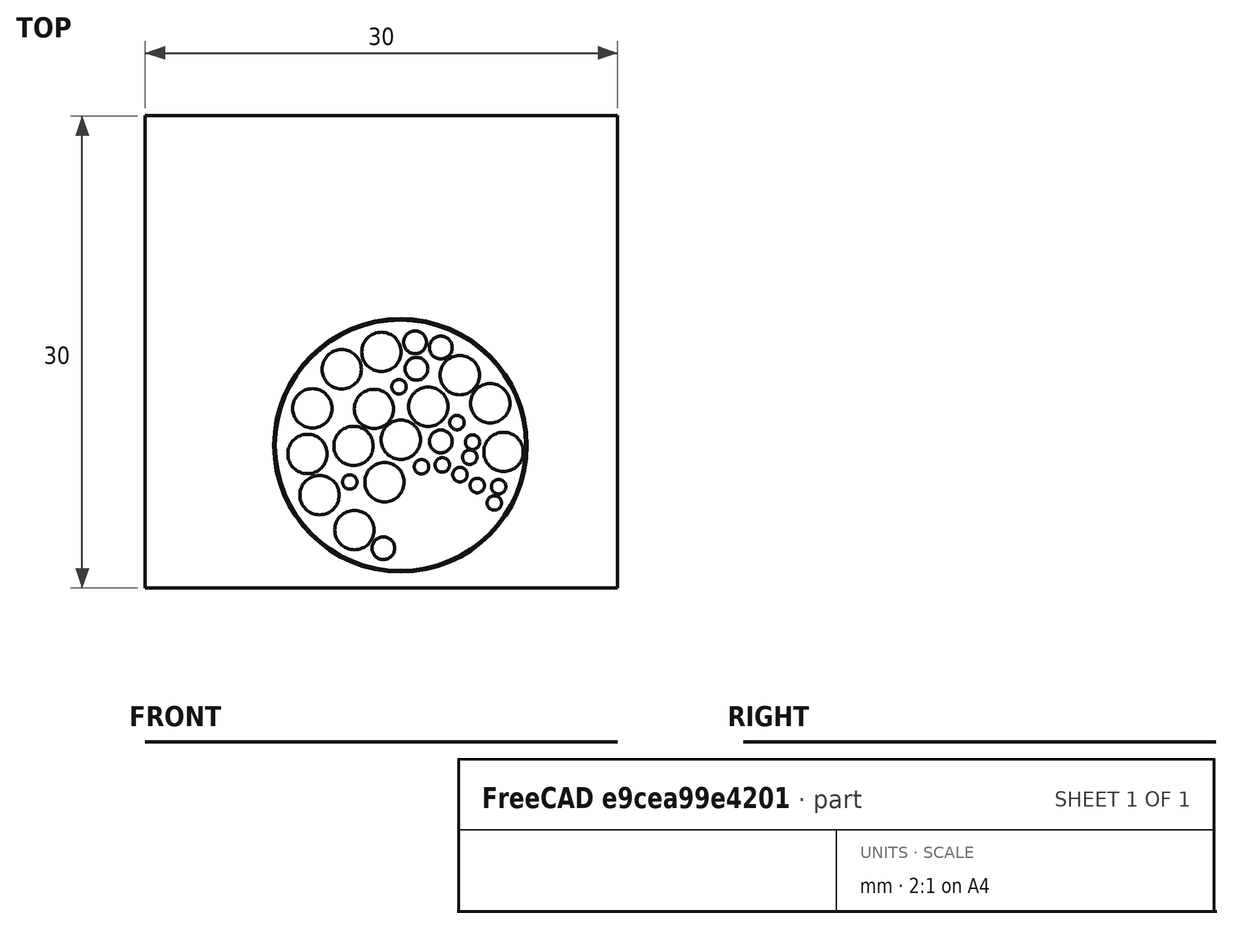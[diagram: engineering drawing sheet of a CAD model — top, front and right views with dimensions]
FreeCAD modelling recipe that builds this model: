
FCSTD DOCUMENT  (FreeCAD 0.21R33668 +26 (Git))
Label: realistic_case_with_dielectrics_fdtd_cell
License: All rights reserved
LicenseURL: http://en.wikipedia.org/wiki/All_rights_reserved
objects: Part::Part2DObjectPython×98, Part::Cut×3, Spreadsheet::Sheet×1, Part::MultiFuse×1
note: 102 computed .brp shape members not serialized (recipe doc carries the construction recipe); baked Part::Feature solids carry a one-line shape summary decoded from their .brp

FEATURE [Part::Part2DObjectPython] Circle006  label="Overbraid_internal"  # Draft 2D object (typed FeaturePython)
  Area = 203.583
  FirstAngle = 0
  LastAngle = 0
  MakeFace = true
  Radius = 8.05
  expr: Radius = <<Spreadsheet>>.OJ_outer_radius
FEATURE [Spreadsheet::Sheet] Spreadsheet
  cells = C1='Radius; D1='Insulation O.R.; G1='Dx; H1='Dy; B2='Overbraid Jacket (OJ); C2(OJ_radius)=7.95; D2(OJ_outer_radius)=8.05; F2='FDTD Cell; G2(fdtd_cell_Lx)==30 mm; H2(FDTD_Cell_Ly)==30 mm; B3='Shield (S); C3(S_radius)==4.5 / 2; F3='Inner region; G3(Inner_region_Dx)=16.5; H3(Inner_region_Dy)==G3; B4='AWG 11; C4(AWG11)==2.3 / 2; D4(awg11_insulation_radius)==C4 + 0.1; G4='Xmax; H4='Xmin; I4='Ymax; J4='Ymin; B5='AWG 17; C5(AWG17)==1.15 / 2; D5(awg17_insulation_radius)==C5 + 0.15; F5='Bounding box; G5==C15 + C4; H5==C12 - C4; I5==D38 + D5; J5==D52 - C3; B6='AWG 21; C6(AWG21)==0.72 / 2; D6(awg21_insulation_radius)==C6 + 0.1; G6==G5 - H5; I6==I5 - J5; A8='Num; B8='AWG 11; C8='x; D8='y; A9=0; B9='A; C9(AWG_11_A_x)==-1.209 mm; D9(AWG_11_A_y)==5.934 mm; A10=1; B10='B; C10(AWG_11_B_x)==-3.734 mm; D10(AWG_11_B_y)=4.83; A11=2; B11='C; C11(AWG_11_C_x)==-5.595; D11(AWG_11_C_y)=2.349; A12=3; B12='D; C12(AWG_11_D_x)==-5.905; D12(AWG_11_D_y)==-0.548; A13=4; B13='E; C13(AWG_11_E_x)==-5.141; D13(AWG_11_E_y)==-3.16; A14=5; B14='F; C14(AWG_11_F_x)==-2.923; D14(AWG_11_F_y)==-5.378; A15=6; B15='G; C15(AWG_11_G_x)=6.545; D15(AWG_11_G_y)==-0.417; A16=7; B16='H; C16(AWG_11_H_x)=5.699; D16(AWG_11_H_y)=2.671; A17=8; B17='I; C17(AWG_11_I_x)=3.767; D17(AWG_11_I_y)=4.46; A18=9; B18='J; C18(AWG_11_J_x)=1.763; D18(AWG_11_J_y)=2.457; A19=10; B19='K; C19(AWG_11_K_x)=0.022; D19(AWG_11_K_y)=0.358; A20=11; B20='L; C20(AWG_11_L_x)==-1.015; D20(AWG_11_L_y)==-2.337; A21=12; B21='M; C21(AWG_11_M_x)=-2.983; D21(AWG_11_M_y)==-0.036; A22=13; B22='N; C22(AWG_11_N_x)=-1.683; D22(AWG_11_N_y)=2.314; A24='Num; B24='AWG 21; C24='x; D24='y; A25=14; B25='A; C25(AWG_21_A_x)==-0.097 mm; D25(AWG_21_A_y)==3.721 mm; A26=15; B26='B; C26(AWG_21_B_x)==-3.221; D26(AWG_21_B_y)==-2.325 mm; A27=16; B27='C; C27(AWG_21_C_x)=1.334; D27(AWG_21_C_y)==-1.359; A28=17; B28='D; C28(AWG_21_D_x)=3.588; D28(AWG_21_D_y)=1.443; A29=18; B29='E; C29(AWG_21_E_x)=4.578; D29(AWG_21_E_y)=0.203; A30=19; B30='F; C30(AWG_21_F_x)=4.399; D30(AWG_21_F_y)==-0.751; A31=20; B31='G; C31(AWG_21_G_x)=2.658; D31(AWG_21_G_y)==-1.24; A32=21; B32='H; C32(AWG_21_H_x)=3.779; D32(AWG_21_H_y)==-1.86; A33=22; B33='I; C33(AWG_21_I_x)=4.876; D33(AWG_21_I_y)==-2.552; A34=23; B34='J; C34(AWG_21_J_x)=6.235; D34(AWG_21_J_y)==-2.623; A35=24; B35='K; C35(AWG_21_K_x)=5.961; D35(AWG_21_K_y)==-3.661; A37='Num; B37='AWG 17; C37='x; D37='y; A38=25; B38='A; C38(AWG_17_A_x)=0.929; D38(AWG_17_A_y)=6.547; A39=26; B39='B; C39(AWG_17_B_x)=2.562; D39(AWG_17_B_y)=6.213; A40=27; B40='C; C40(AWG_17_C_x)=1.012; D40(AWG_17_C_y)=4.866; A41=28; B41='D; C41(AWG_17_D_x)=2.562; D41(AWG_17_D_y)=0.251; A42=29; B42='E; C42(AWG_17_E_x)==-1.087; D42(AWG_17_E_y)==-6.535; A43=30; B43='S; C43(Shield_x)=2.336; D43(Shield_y)==-4.901; A45='Num; B45='AWG 17 within shield; C45='x; D45='y; A46=31; B46='F; C46=2.276; D46==-3.458; A47=32; B47='G; C47=0.893; D47==-4.412; A48=33; B48='H; C48=1.155; D48==-5.712; A49=34; B49='I; C49=2.431; D49==-6.332; A50=35; B50='J; C50=3.659; D50==-5.533; A51=36; B51='K; C51=3.648; D51==-4.198; A52=37; +3 more cells
FEATURE [Part::Part2DObjectPython] Circle017  label="Conductor_000"  # Draft 2D object (typed FeaturePython)
  Area = 4.15476
  FirstAngle = 0
  LastAngle = 0
  MakeFace = true
  Placement = pos=(-1.209,5.934,0) rot=(-1.209,5.934,1;0rad)
  Radius = 1.15
  expr: .Placement.Base.x = <<Spreadsheet>>.AWG_11_A_x
  expr: .Placement.Base.y = <<Spreadsheet>>.AWG_11_A_y
  expr: .Placement.Rotation.Axis.x = <<Spreadsheet>>.AWG_11_A_x
  expr: .Placement.Rotation.Axis.y = <<Spreadsheet>>.AWG_11_A_y
  expr: Radius = <<Spreadsheet>>.AWG11
FEATURE [Part::Part2DObjectPython] Circle018  label="Conductor_001"  # Draft 2D object (typed FeaturePython)
  Area = 4.15476
  FirstAngle = 0
  LastAngle = 0
  MakeFace = true
  Placement = pos=(-3.734,4.83,0) rot=(-1.209,5.934,1;0rad)
  Radius = 1.15
  expr: .Placement.Base.x = <<Spreadsheet>>.AWG_11_B_x
  expr: .Placement.Base.y = <<Spreadsheet>>.AWG_11_B_y
  expr: .Placement.Rotation.Axis.x = <<Spreadsheet>>.AWG_11_A_x
  expr: .Placement.Rotation.Axis.y = <<Spreadsheet>>.AWG_11_A_y
  expr: Radius = <<Spreadsheet>>.AWG11
FEATURE [Part::Part2DObjectPython] Circle019  label="Conductor_002"  # Draft 2D object (typed FeaturePython)
  Area = 4.15476
  FirstAngle = 0
  LastAngle = 0
  MakeFace = true
  Placement = pos=(-5.595,2.349,0) rot=(-1.209,5.934,1;0rad)
  Radius = 1.15
  expr: .Placement.Base.x = <<Spreadsheet>>.AWG_11_C_x
  expr: .Placement.Base.y = <<Spreadsheet>>.AWG_11_C_y
  expr: .Placement.Rotation.Axis.x = <<Spreadsheet>>.AWG_11_A_x
  expr: .Placement.Rotation.Axis.y = <<Spreadsheet>>.AWG_11_A_y
  expr: Radius = <<Spreadsheet>>.AWG11
FEATURE [Part::Part2DObjectPython] Circle020  label="Conductor_003"  # Draft 2D object (typed FeaturePython)
  Area = 4.15476
  FirstAngle = 0
  LastAngle = 0
  MakeFace = true
  Placement = pos=(-5.905,-0.548,0) rot=(-1.209,5.934,1;0rad)
  Radius = 1.15
  expr: .Placement.Base.x = <<Spreadsheet>>.AWG_11_D_x
  expr: .Placement.Base.y = <<Spreadsheet>>.AWG_11_D_y
  expr: .Placement.Rotation.Axis.x = <<Spreadsheet>>.AWG_11_A_x
  expr: .Placement.Rotation.Axis.y = <<Spreadsheet>>.AWG_11_A_y
  expr: Radius = <<Spreadsheet>>.AWG11
FEATURE [Part::Part2DObjectPython] Circle021  label="Conductor_004"  # Draft 2D object (typed FeaturePython)
  Area = 4.15476
  FirstAngle = 0
  LastAngle = 0
  MakeFace = true
  Placement = pos=(-5.141,-3.16,0) rot=(-1.209,5.934,1;0rad)
  Radius = 1.15
  expr: .Placement.Base.x = <<Spreadsheet>>.AWG_11_E_x
  expr: .Placement.Base.y = <<Spreadsheet>>.AWG_11_E_y
  expr: .Placement.Rotation.Axis.x = <<Spreadsheet>>.AWG_11_A_x
  expr: .Placement.Rotation.Axis.y = <<Spreadsheet>>.AWG_11_A_y
  expr: Radius = <<Spreadsheet>>.AWG11
FEATURE [Part::Part2DObjectPython] Circle022  label="Conductor_005"  # Draft 2D object (typed FeaturePython)
  Area = 4.15476
  FirstAngle = 0
  LastAngle = 0
  MakeFace = true
  Placement = pos=(-2.923,-5.378,0) rot=(-1.209,5.934,1;0rad)
  Radius = 1.15
  expr: .Placement.Base.x = <<Spreadsheet>>.AWG_11_F_x
  expr: .Placement.Base.y = <<Spreadsheet>>.AWG_11_F_y
  expr: .Placement.Rotation.Axis.x = <<Spreadsheet>>.AWG_11_A_x
  expr: .Placement.Rotation.Axis.y = <<Spreadsheet>>.AWG_11_A_y
  expr: Radius = <<Spreadsheet>>.AWG11
FEATURE [Part::Part2DObjectPython] Circle023  label="Conductor_006"  # Draft 2D object (typed FeaturePython)
  Area = 4.15476
  FirstAngle = 0
  LastAngle = 0
  MakeFace = true
  Placement = pos=(6.545,-0.417,0) rot=(-1.209,5.934,1;0rad)
  Radius = 1.15
  expr: .Placement.Base.x = <<Spreadsheet>>.AWG_11_G_x
  expr: .Placement.Base.y = <<Spreadsheet>>.AWG_11_G_y
  expr: .Placement.Rotation.Axis.x = <<Spreadsheet>>.AWG_11_A_x
  expr: .Placement.Rotation.Axis.y = <<Spreadsheet>>.AWG_11_A_y
  expr: Radius = <<Spreadsheet>>.AWG11
FEATURE [Part::Part2DObjectPython] Circle024  label="Conductor_007"  # Draft 2D object (typed FeaturePython)
  Area = 4.15476
  FirstAngle = 0
  LastAngle = 0
  MakeFace = true
  Placement = pos=(5.699,2.671,0) rot=(-1.209,5.934,1;0rad)
  Radius = 1.15
  expr: .Placement.Base.x = <<Spreadsheet>>.AWG_11_H_x
  expr: .Placement.Base.y = <<Spreadsheet>>.AWG_11_H_y
  expr: .Placement.Rotation.Axis.x = <<Spreadsheet>>.AWG_11_A_x
  expr: .Placement.Rotation.Axis.y = <<Spreadsheet>>.AWG_11_A_y
  expr: Radius = <<Spreadsheet>>.AWG11
FEATURE [Part::Part2DObjectPython] Circle025  label="Conductor_008"  # Draft 2D object (typed FeaturePython)
  Area = 4.15476
  FirstAngle = 0
  LastAngle = 0
  MakeFace = true
  Placement = pos=(3.767,4.46,0) rot=(-1.209,5.934,1;0rad)
  Radius = 1.15
  expr: .Placement.Base.x = <<Spreadsheet>>.AWG_11_I_x
  expr: .Placement.Base.y = <<Spreadsheet>>.AWG_11_I_y
  expr: .Placement.Rotation.Axis.x = <<Spreadsheet>>.AWG_11_A_x
  expr: .Placement.Rotation.Axis.y = <<Spreadsheet>>.AWG_11_A_y
  expr: Radius = <<Spreadsheet>>.AWG11
FEATURE [Part::Part2DObjectPython] Circle026  label="Conductor_009"  # Draft 2D object (typed FeaturePython)
  Area = 4.15476
  FirstAngle = 0
  LastAngle = 0
  MakeFace = true
  Placement = pos=(1.763,2.457,0) rot=(-1.209,5.934,1;0rad)
  Radius = 1.15
  expr: .Placement.Base.x = <<Spreadsheet>>.AWG_11_J_x
  expr: .Placement.Base.y = <<Spreadsheet>>.AWG_11_J_y
  expr: .Placement.Rotation.Axis.x = <<Spreadsheet>>.AWG_11_A_x
  expr: .Placement.Rotation.Axis.y = <<Spreadsheet>>.AWG_11_A_y
  expr: Radius = <<Spreadsheet>>.AWG11
FEATURE [Part::Part2DObjectPython] Circle027  label="Conductor_010"  # Draft 2D object (typed FeaturePython)
  Area = 4.15476
  FirstAngle = 0
  LastAngle = 0
  MakeFace = true
  Placement = pos=(0.022,0.358,0) rot=(-1.209,5.934,1;0rad)
  Radius = 1.15
  expr: .Placement.Base.x = <<Spreadsheet>>.AWG_11_K_x
  expr: .Placement.Base.y = <<Spreadsheet>>.AWG_11_K_y
  expr: .Placement.Rotation.Axis.x = <<Spreadsheet>>.AWG_11_A_x
  expr: .Placement.Rotation.Axis.y = <<Spreadsheet>>.AWG_11_A_y
  expr: Radius = <<Spreadsheet>>.AWG11
FEATURE [Part::Part2DObjectPython] Circle028  label="Conductor_011"  # Draft 2D object (typed FeaturePython)
  Area = 4.15476
  FirstAngle = 0
  LastAngle = 0
  MakeFace = true
  Placement = pos=(-1.015,-2.337,0) rot=(-1.209,5.934,1;0rad)
  Radius = 1.15
  expr: .Placement.Base.x = <<Spreadsheet>>.AWG_11_L_x
  expr: .Placement.Base.y = <<Spreadsheet>>.AWG_11_L_y
  expr: .Placement.Rotation.Axis.x = <<Spreadsheet>>.AWG_11_A_x
  expr: .Placement.Rotation.Axis.y = <<Spreadsheet>>.AWG_11_A_y
  expr: Radius = <<Spreadsheet>>.AWG11
FEATURE [Part::Part2DObjectPython] Circle029  label="Conductor_012"  # Draft 2D object (typed FeaturePython)
  Area = 4.15476
  FirstAngle = 0
  LastAngle = 0
  MakeFace = true
  Placement = pos=(-2.983,-0.036,0) rot=(-1.209,5.934,1;0rad)
  Radius = 1.15
  expr: .Placement.Base.x = <<Spreadsheet>>.AWG_11_M_x
  expr: .Placement.Base.y = <<Spreadsheet>>.AWG_11_M_y
  expr: .Placement.Rotation.Axis.x = <<Spreadsheet>>.AWG_11_A_x
  expr: .Placement.Rotation.Axis.y = <<Spreadsheet>>.AWG_11_A_y
  expr: Radius = <<Spreadsheet>>.AWG11
FEATURE [Part::Part2DObjectPython] Circle030  label="Conductor_013"  # Draft 2D object (typed FeaturePython)
  Area = 4.15476
  FirstAngle = 0
  LastAngle = 0
  MakeFace = true
  Placement = pos=(-1.683,2.314,0) rot=(-1.209,5.934,1;0rad)
  Radius = 1.15
  expr: .Placement.Base.x = <<Spreadsheet>>.AWG_11_N_x
  expr: .Placement.Base.y = <<Spreadsheet>>.AWG_11_N_y
  expr: .Placement.Rotation.Axis.x = <<Spreadsheet>>.AWG_11_A_x
  expr: .Placement.Rotation.Axis.y = <<Spreadsheet>>.AWG_11_A_y
  expr: Radius = <<Spreadsheet>>.AWG11
FEATURE [Part::Part2DObjectPython] Circle031  label="Conductor_014"  # Draft 2D object (typed FeaturePython)
  Area = 0.40715
  FirstAngle = 0
  LastAngle = 0
  MakeFace = true
  Placement = pos=(-0.097,3.721,0) rot=(-1.209,5.934,1;0rad)
  Radius = 0.36
  expr: .Placement.Base.x = <<Spreadsheet>>.AWG_21_A_x
  expr: .Placement.Base.y = <<Spreadsheet>>.AWG_21_A_y
  expr: .Placement.Rotation.Axis.x = <<Spreadsheet>>.AWG_11_A_x
  expr: .Placement.Rotation.Axis.y = <<Spreadsheet>>.AWG_11_A_y
  expr: Radius = <<Spreadsheet>>.AWG21
FEATURE [Part::Part2DObjectPython] Circle032  label="Conductor_015"  # Draft 2D object (typed FeaturePython)
  Area = 0.40715
  FirstAngle = 0
  LastAngle = 0
  MakeFace = true
  Placement = pos=(-3.221,-2.325,0) rot=(-1.209,5.934,1;0rad)
  Radius = 0.36
  expr: .Placement.Base.x = <<Spreadsheet>>.AWG_21_B_x
  expr: .Placement.Base.y = <<Spreadsheet>>.AWG_21_B_y
  expr: .Placement.Rotation.Axis.x = <<Spreadsheet>>.AWG_11_A_x
  expr: .Placement.Rotation.Axis.y = <<Spreadsheet>>.AWG_11_A_y
  expr: Radius = <<Spreadsheet>>.AWG21
FEATURE [Part::Part2DObjectPython] Circle033  label="Conductor_016"  # Draft 2D object (typed FeaturePython)
  Area = 0.40715
  FirstAngle = 0
  LastAngle = 0
  MakeFace = true
  Placement = pos=(1.334,-1.359,0) rot=(-1.209,5.934,1;0rad)
  Radius = 0.36
  expr: .Placement.Base.x = <<Spreadsheet>>.AWG_21_C_x
  expr: .Placement.Base.y = <<Spreadsheet>>.AWG_21_C_y
  expr: .Placement.Rotation.Axis.x = <<Spreadsheet>>.AWG_11_A_x
  expr: .Placement.Rotation.Axis.y = <<Spreadsheet>>.AWG_11_A_y
  expr: Radius = <<Spreadsheet>>.AWG21
FEATURE [Part::Part2DObjectPython] Circle034  label="Conductor_017"  # Draft 2D object (typed FeaturePython)
  Area = 0.40715
  FirstAngle = 0
  LastAngle = 0
  MakeFace = true
  Placement = pos=(3.588,1.443,0) rot=(-1.209,5.934,1;0rad)
  Radius = 0.36
  expr: .Placement.Base.x = <<Spreadsheet>>.AWG_21_D_x
  expr: .Placement.Base.y = <<Spreadsheet>>.AWG_21_D_y
  expr: .Placement.Rotation.Axis.x = <<Spreadsheet>>.AWG_11_A_x
  expr: .Placement.Rotation.Axis.y = <<Spreadsheet>>.AWG_11_A_y
  expr: Radius = <<Spreadsheet>>.AWG21
FEATURE [Part::Part2DObjectPython] Circle035  label="Conductor_018"  # Draft 2D object (typed FeaturePython)
  Area = 0.40715
  FirstAngle = 0
  LastAngle = 0
  MakeFace = true
  Placement = pos=(4.578,0.203,0) rot=(-1.209,5.934,1;0rad)
  Radius = 0.36
  expr: .Placement.Base.x = <<Spreadsheet>>.AWG_21_E_x
  expr: .Placement.Base.y = <<Spreadsheet>>.AWG_21_E_y
  expr: .Placement.Rotation.Axis.x = <<Spreadsheet>>.AWG_11_A_x
  expr: .Placement.Rotation.Axis.y = <<Spreadsheet>>.AWG_11_A_y
  expr: Radius = <<Spreadsheet>>.AWG21
FEATURE [Part::Part2DObjectPython] Circle036  label="Conductor_019"  # Draft 2D object (typed FeaturePython)
  Area = 0.40715
  FirstAngle = 0
  LastAngle = 0
  MakeFace = true
  Placement = pos=(4.399,-0.751,0) rot=(-1.209,5.934,1;0rad)
  Radius = 0.36
  expr: .Placement.Base.x = <<Spreadsheet>>.AWG_21_F_x
  expr: .Placement.Base.y = <<Spreadsheet>>.AWG_21_F_y
  expr: .Placement.Rotation.Axis.x = <<Spreadsheet>>.AWG_11_A_x
  expr: .Placement.Rotation.Axis.y = <<Spreadsheet>>.AWG_11_A_y
  expr: Radius = <<Spreadsheet>>.AWG21
FEATURE [Part::Part2DObjectPython] Circle037  label="Conductor_020"  # Draft 2D object (typed FeaturePython)
  Area = 0.40715
  FirstAngle = 0
  LastAngle = 0
  MakeFace = true
  Placement = pos=(2.658,-1.24,0) rot=(-1.209,5.934,1;0rad)
  Radius = 0.36
  expr: .Placement.Base.x = <<Spreadsheet>>.AWG_21_G_x
  expr: .Placement.Base.y = <<Spreadsheet>>.AWG_21_G_y
  expr: .Placement.Rotation.Axis.x = <<Spreadsheet>>.AWG_11_A_x
  expr: .Placement.Rotation.Axis.y = <<Spreadsheet>>.AWG_11_A_y
  expr: Radius = <<Spreadsheet>>.AWG21
FEATURE [Part::Part2DObjectPython] Circle038  label="Conductor_021"  # Draft 2D object (typed FeaturePython)
  Area = 0.40715
  FirstAngle = 0
  LastAngle = 0
  MakeFace = true
  Placement = pos=(3.779,-1.86,0) rot=(-1.209,5.934,1;0rad)
  Radius = 0.36
  expr: .Placement.Base.x = <<Spreadsheet>>.AWG_21_H_x
  expr: .Placement.Base.y = <<Spreadsheet>>.AWG_21_H_y
  expr: .Placement.Rotation.Axis.x = <<Spreadsheet>>.AWG_11_A_x
  expr: .Placement.Rotation.Axis.y = <<Spreadsheet>>.AWG_11_A_y
  expr: Radius = <<Spreadsheet>>.AWG21
FEATURE [Part::Part2DObjectPython] Circle039  label="Conductor_022"  # Draft 2D object (typed FeaturePython)
  Area = 0.40715
  FirstAngle = 0
  LastAngle = 0
  MakeFace = true
  Placement = pos=(4.876,-2.552,0) rot=(-1.209,5.934,1;0rad)
  Radius = 0.36
  expr: .Placement.Base.x = <<Spreadsheet>>.AWG_21_I_x
  expr: .Placement.Base.y = <<Spreadsheet>>.AWG_21_I_y
  expr: .Placement.Rotation.Axis.x = <<Spreadsheet>>.AWG_11_A_x
  expr: .Placement.Rotation.Axis.y = <<Spreadsheet>>.AWG_11_A_y
  expr: Radius = <<Spreadsheet>>.AWG21
FEATURE [Part::Part2DObjectPython] Circle040  label="Conductor_023"  # Draft 2D object (typed FeaturePython)
  Area = 0.40715
  FirstAngle = 0
  LastAngle = 0
  MakeFace = true
  Placement = pos=(6.235,-2.623,0) rot=(-1.209,5.934,1;0rad)
  Radius = 0.36
  expr: .Placement.Base.x = <<Spreadsheet>>.AWG_21_J_x
  expr: .Placement.Base.y = <<Spreadsheet>>.AWG_21_J_y
  expr: .Placement.Rotation.Axis.x = <<Spreadsheet>>.AWG_11_A_x
  expr: .Placement.Rotation.Axis.y = <<Spreadsheet>>.AWG_11_A_y
  expr: Radius = <<Spreadsheet>>.AWG21
FEATURE [Part::Part2DObjectPython] Circle041  label="Conductor_024"  # Draft 2D object (typed FeaturePython)
  Area = 0.40715
  FirstAngle = 0
  LastAngle = 0
  MakeFace = true
  Placement = pos=(5.961,-3.661,0) rot=(-1.209,5.934,1;0rad)
  Radius = 0.36
  expr: .Placement.Base.x = <<Spreadsheet>>.AWG_21_K_x
  expr: .Placement.Base.y = <<Spreadsheet>>.AWG_21_K_y
  expr: .Placement.Rotation.Axis.x = <<Spreadsheet>>.AWG_11_A_x
  expr: .Placement.Rotation.Axis.y = <<Spreadsheet>>.AWG_11_A_y
  expr: Radius = <<Spreadsheet>>.AWG21
FEATURE [Part::Part2DObjectPython] Circle042  label="Conductor_025"  # Draft 2D object (typed FeaturePython)
  Area = 1.03869
  FirstAngle = 0
  LastAngle = 0
  MakeFace = true
  Placement = pos=(0.929,6.547,0) rot=(-1.209,5.934,1;0rad)
  Radius = 0.575
  expr: .Placement.Base.x = <<Spreadsheet>>.AWG_17_A_x
  expr: .Placement.Base.y = <<Spreadsheet>>.AWG_17_A_y
  expr: .Placement.Rotation.Axis.x = <<Spreadsheet>>.AWG_11_A_x
  expr: .Placement.Rotation.Axis.y = <<Spreadsheet>>.AWG_11_A_y
  expr: Radius = <<Spreadsheet>>.AWG17
FEATURE [Part::Part2DObjectPython] Circle043  label="Conductor_026"  # Draft 2D object (typed FeaturePython)
  Area = 1.03869
  FirstAngle = 0
  LastAngle = 0
  MakeFace = true
  Placement = pos=(2.562,6.213,0) rot=(-1.209,5.934,1;0rad)
  Radius = 0.575
  expr: .Placement.Base.x = <<Spreadsheet>>.AWG_17_B_x
  expr: .Placement.Base.y = <<Spreadsheet>>.AWG_17_B_y
  expr: .Placement.Rotation.Axis.x = <<Spreadsheet>>.AWG_11_A_x
  expr: .Placement.Rotation.Axis.y = <<Spreadsheet>>.AWG_11_A_y
  expr: Radius = <<Spreadsheet>>.AWG17
FEATURE [Part::Part2DObjectPython] Circle044  label="Conductor_027"  # Draft 2D object (typed FeaturePython)
  Area = 1.03869
  FirstAngle = 0
  LastAngle = 0
  MakeFace = true
  Placement = pos=(1.012,4.866,0) rot=(-1.209,5.934,1;0rad)
  Radius = 0.575
  expr: .Placement.Base.x = <<Spreadsheet>>.AWG_17_C_x
  expr: .Placement.Base.y = <<Spreadsheet>>.AWG_17_C_y
  expr: .Placement.Rotation.Axis.x = <<Spreadsheet>>.AWG_11_A_x
  expr: .Placement.Rotation.Axis.y = <<Spreadsheet>>.AWG_11_A_y
  expr: Radius = <<Spreadsheet>>.AWG17
FEATURE [Part::Part2DObjectPython] Circle045  label="Conductor_028"  # Draft 2D object (typed FeaturePython)
  Area = 1.03869
  FirstAngle = 0
  LastAngle = 0
  MakeFace = true
  Placement = pos=(2.562,0.251,0) rot=(-1.209,5.934,1;0rad)
  Radius = 0.575
  expr: .Placement.Base.x = <<Spreadsheet>>.AWG_17_D_x
  expr: .Placement.Base.y = <<Spreadsheet>>.AWG_17_D_y
  expr: .Placement.Rotation.Axis.x = <<Spreadsheet>>.AWG_11_A_x
  expr: .Placement.Rotation.Axis.y = <<Spreadsheet>>.AWG_11_A_y
  expr: Radius = <<Spreadsheet>>.AWG17
FEATURE [Part::Part2DObjectPython] Circle046  label="Conductor_029"  # Draft 2D object (typed FeaturePython)
  Area = 1.03869
  FirstAngle = 0
  LastAngle = 0
  MakeFace = true
  Placement = pos=(-1.087,-6.535,0) rot=(-1.209,5.934,1;0rad)
  Radius = 0.575
  expr: .Placement.Base.x = <<Spreadsheet>>.AWG_17_E_x
  expr: .Placement.Base.y = <<Spreadsheet>>.AWG_17_E_y
  expr: .Placement.Rotation.Axis.x = <<Spreadsheet>>.AWG_11_A_x
  expr: .Placement.Rotation.Axis.y = <<Spreadsheet>>.AWG_11_A_y
  expr: Radius = <<Spreadsheet>>.AWG17
FEATURE [Part::Part2DObjectPython] Circle047  label="Conductor_030"  # Draft 2D object (typed FeaturePython)
  Area = 15.9043
  FirstAngle = 0
  LastAngle = 0
  MakeFace = true
  Placement = pos=(2.336,-4.901,0) rot=(-1.209,5.934,1;0rad)
  Radius = 2.25
  expr: .Placement.Base.x = Spreadsheet.Shield_x
  expr: .Placement.Base.y = Spreadsheet.Shield_y
  expr: .Placement.Rotation.Axis.x = <<Spreadsheet>>.AWG_11_A_x
  expr: .Placement.Rotation.Axis.y = <<Spreadsheet>>.AWG_11_A_y
  expr: Radius = <<Spreadsheet>>.S_radius
FEATURE [Part::Part2DObjectPython] Circle048  label="Dielectric_000"  # Draft 2D object (typed FeaturePython)
  Area = 4.90874
  FirstAngle = 0
  LastAngle = 0
  MakeFace = true
  Placement = pos=(-1.209,5.934,0) rot=(-1.209,5.934,1;0rad)
  Radius = 1.25
  expr: .Placement.Base.x = <<Spreadsheet>>.AWG_11_A_x
  expr: .Placement.Base.y = <<Spreadsheet>>.AWG_11_A_y
  expr: .Placement.Rotation.Axis.x = <<Spreadsheet>>.AWG_11_A_x
  expr: .Placement.Rotation.Axis.y = <<Spreadsheet>>.AWG_11_A_y
  expr: Radius = <<Spreadsheet>>.awg11_insulation_radius
FEATURE [Part::Part2DObjectPython] Circle049  label="Dielectric_001"  # Draft 2D object (typed FeaturePython)
  Area = 4.90874
  FirstAngle = 0
  LastAngle = 0
  MakeFace = true
  Placement = pos=(-3.734,4.83,0) rot=(-1.209,5.934,1;0rad)
  Radius = 1.25
  expr: .Placement.Base.x = <<Spreadsheet>>.AWG_11_B_x
  expr: .Placement.Base.y = <<Spreadsheet>>.AWG_11_B_y
  expr: .Placement.Rotation.Axis.x = <<Spreadsheet>>.AWG_11_A_x
  expr: .Placement.Rotation.Axis.y = <<Spreadsheet>>.AWG_11_A_y
  expr: Radius = <<Spreadsheet>>.awg11_insulation_radius
FEATURE [Part::Part2DObjectPython] Circle050  label="Dielectric_002"  # Draft 2D object (typed FeaturePython)
  Area = 4.90874
  FirstAngle = 0
  LastAngle = 0
  MakeFace = true
  Placement = pos=(-5.595,2.349,0) rot=(-1.209,5.934,1;0rad)
  Radius = 1.25
  expr: .Placement.Base.x = <<Spreadsheet>>.AWG_11_C_x
  expr: .Placement.Base.y = <<Spreadsheet>>.AWG_11_C_y
  expr: .Placement.Rotation.Axis.x = <<Spreadsheet>>.AWG_11_A_x
  expr: .Placement.Rotation.Axis.y = <<Spreadsheet>>.AWG_11_A_y
  expr: Radius = <<Spreadsheet>>.awg11_insulation_radius
FEATURE [Part::Part2DObjectPython] Circle051  label="Dielectric_003"  # Draft 2D object (typed FeaturePython)
  Area = 4.90874
  FirstAngle = 0
  LastAngle = 0
  MakeFace = true
  Placement = pos=(-5.905,-0.548,0) rot=(-1.209,5.934,1;0rad)
  Radius = 1.25
  expr: .Placement.Base.x = <<Spreadsheet>>.AWG_11_D_x
  expr: .Placement.Base.y = <<Spreadsheet>>.AWG_11_D_y
  expr: .Placement.Rotation.Axis.x = <<Spreadsheet>>.AWG_11_A_x
  expr: .Placement.Rotation.Axis.y = <<Spreadsheet>>.AWG_11_A_y
  expr: Radius = <<Spreadsheet>>.awg11_insulation_radius
FEATURE [Part::Part2DObjectPython] Circle052  label="Dielectric_004"  # Draft 2D object (typed FeaturePython)
  Area = 4.90874
  FirstAngle = 0
  LastAngle = 0
  MakeFace = true
  Placement = pos=(-5.141,-3.16,0) rot=(-1.209,5.934,1;0rad)
  Radius = 1.25
  expr: .Placement.Base.x = <<Spreadsheet>>.AWG_11_E_x
  expr: .Placement.Base.y = <<Spreadsheet>>.AWG_11_E_y
  expr: .Placement.Rotation.Axis.x = <<Spreadsheet>>.AWG_11_A_x
  expr: .Placement.Rotation.Axis.y = <<Spreadsheet>>.AWG_11_A_y
  expr: Radius = <<Spreadsheet>>.awg11_insulation_radius
FEATURE [Part::Part2DObjectPython] Circle053  label="Dielectric_005"  # Draft 2D object (typed FeaturePython)
  Area = 4.90874
  FirstAngle = 0
  LastAngle = 0
  MakeFace = true
  Placement = pos=(-2.923,-5.378,0) rot=(-1.209,5.934,1;0rad)
  Radius = 1.25
  expr: .Placement.Base.x = <<Spreadsheet>>.AWG_11_F_x
  expr: .Placement.Base.y = <<Spreadsheet>>.AWG_11_F_y
  expr: .Placement.Rotation.Axis.x = <<Spreadsheet>>.AWG_11_A_x
  expr: .Placement.Rotation.Axis.y = <<Spreadsheet>>.AWG_11_A_y
  expr: Radius = <<Spreadsheet>>.awg11_insulation_radius
FEATURE [Part::Part2DObjectPython] Circle054  label="Dielectric_006"  # Draft 2D object (typed FeaturePython)
  Area = 4.90874
  FirstAngle = 0
  LastAngle = 0
  MakeFace = true
  Placement = pos=(6.545,-0.417,0) rot=(-1.209,5.934,1;0rad)
  Radius = 1.25
  expr: .Placement.Base.x = <<Spreadsheet>>.AWG_11_G_x
  expr: .Placement.Base.y = <<Spreadsheet>>.AWG_11_G_y
  expr: .Placement.Rotation.Axis.x = <<Spreadsheet>>.AWG_11_A_x
  expr: .Placement.Rotation.Axis.y = <<Spreadsheet>>.AWG_11_A_y
  expr: Radius = <<Spreadsheet>>.awg11_insulation_radius
FEATURE [Part::Part2DObjectPython] Circle055  label="Dielectric_007"  # Draft 2D object (typed FeaturePython)
  Area = 4.90874
  FirstAngle = 0
  LastAngle = 0
  MakeFace = true
  Placement = pos=(5.699,2.671,0) rot=(-1.209,5.934,1;0rad)
  Radius = 1.25
  expr: .Placement.Base.x = <<Spreadsheet>>.AWG_11_H_x
  expr: .Placement.Base.y = <<Spreadsheet>>.AWG_11_H_y
  expr: .Placement.Rotation.Axis.x = <<Spreadsheet>>.AWG_11_A_x
  expr: .Placement.Rotation.Axis.y = <<Spreadsheet>>.AWG_11_A_y
  expr: Radius = <<Spreadsheet>>.awg11_insulation_radius
FEATURE [Part::Part2DObjectPython] Circle056  label="Dielectric_008"  # Draft 2D object (typed FeaturePython)
  Area = 4.90874
  FirstAngle = 0
  LastAngle = 0
  MakeFace = true
  Placement = pos=(3.767,4.46,0) rot=(-1.209,5.934,1;0rad)
  Radius = 1.25
  expr: .Placement.Base.x = <<Spreadsheet>>.AWG_11_I_x
  expr: .Placement.Base.y = <<Spreadsheet>>.AWG_11_I_y
  expr: .Placement.Rotation.Axis.x = <<Spreadsheet>>.AWG_11_A_x
  expr: .Placement.Rotation.Axis.y = <<Spreadsheet>>.AWG_11_A_y
  expr: Radius = <<Spreadsheet>>.awg11_insulation_radius
FEATURE [Part::Part2DObjectPython] Circle057  label="Dielectric_009"  # Draft 2D object (typed FeaturePython)
  Area = 4.90874
  FirstAngle = 0
  LastAngle = 0
  MakeFace = true
  Placement = pos=(1.763,2.457,0) rot=(-1.209,5.934,1;0rad)
  Radius = 1.25
  expr: .Placement.Base.x = <<Spreadsheet>>.AWG_11_J_x
  expr: .Placement.Base.y = <<Spreadsheet>>.AWG_11_J_y
  expr: .Placement.Rotation.Axis.x = <<Spreadsheet>>.AWG_11_A_x
  expr: .Placement.Rotation.Axis.y = <<Spreadsheet>>.AWG_11_A_y
  expr: Radius = <<Spreadsheet>>.awg11_insulation_radius
FEATURE [Part::Part2DObjectPython] Circle058  label="Dielectric_010"  # Draft 2D object (typed FeaturePython)
  Area = 4.90874
  FirstAngle = 0
  LastAngle = 0
  MakeFace = true
  Placement = pos=(0.022,0.358,0) rot=(-1.209,5.934,1;0rad)
  Radius = 1.25
  expr: .Placement.Base.x = <<Spreadsheet>>.AWG_11_K_x
  expr: .Placement.Base.y = <<Spreadsheet>>.AWG_11_K_y
  expr: .Placement.Rotation.Axis.x = <<Spreadsheet>>.AWG_11_A_x
  expr: .Placement.Rotation.Axis.y = <<Spreadsheet>>.AWG_11_A_y
  expr: Radius = <<Spreadsheet>>.awg11_insulation_radius
FEATURE [Part::Part2DObjectPython] Circle059  label="Dielectric_011"  # Draft 2D object (typed FeaturePython)
  Area = 4.90874
  FirstAngle = 0
  LastAngle = 0
  MakeFace = true
  Placement = pos=(-1.015,-2.337,0) rot=(-1.209,5.934,1;0rad)
  Radius = 1.25
  expr: .Placement.Base.x = <<Spreadsheet>>.AWG_11_L_x
  expr: .Placement.Base.y = <<Spreadsheet>>.AWG_11_L_y
  expr: .Placement.Rotation.Axis.x = <<Spreadsheet>>.AWG_11_A_x
  expr: .Placement.Rotation.Axis.y = <<Spreadsheet>>.AWG_11_A_y
  expr: Radius = <<Spreadsheet>>.awg11_insulation_radius
FEATURE [Part::Part2DObjectPython] Circle060  label="Dielectric_012"  # Draft 2D object (typed FeaturePython)
  Area = 4.90874
  FirstAngle = 0
  LastAngle = 0
  MakeFace = true
  Placement = pos=(-2.983,-0.036,0) rot=(-1.209,5.934,1;0rad)
  Radius = 1.25
  expr: .Placement.Base.x = <<Spreadsheet>>.AWG_11_M_x
  expr: .Placement.Base.y = <<Spreadsheet>>.AWG_11_M_y
  expr: .Placement.Rotation.Axis.x = <<Spreadsheet>>.AWG_11_A_x
  expr: .Placement.Rotation.Axis.y = <<Spreadsheet>>.AWG_11_A_y
  expr: Radius = <<Spreadsheet>>.awg11_insulation_radius
FEATURE [Part::Part2DObjectPython] Circle061  label="Dielectric_013"  # Draft 2D object (typed FeaturePython)
  Area = 4.90874
  FirstAngle = 0
  LastAngle = 0
  MakeFace = true
  Placement = pos=(-1.683,2.314,0) rot=(-1.209,5.934,1;0rad)
  Radius = 1.25
  expr: .Placement.Base.x = <<Spreadsheet>>.AWG_11_N_x
  expr: .Placement.Base.y = <<Spreadsheet>>.AWG_11_N_y
  expr: .Placement.Rotation.Axis.x = <<Spreadsheet>>.AWG_11_A_x
  expr: .Placement.Rotation.Axis.y = <<Spreadsheet>>.AWG_11_A_y
  expr: Radius = <<Spreadsheet>>.awg11_insulation_radius
FEATURE [Part::Part2DObjectPython] Circle062  label="Overbraid_external"  # Draft 2D object (typed FeaturePython)
  Area = 198.557
  FirstAngle = 0
  LastAngle = 0
  MakeFace = true
  Radius = 7.95
  expr: Radius = <<Spreadsheet>>.OJ_radius
FEATURE [Part::Cut] Cut  label="Dielectric_030"
  Base = -> Circle006
  Tool = -> Circle062
FEATURE [Part::Part2DObjectPython] Circle063  label="Dielectric_014"  # Draft 2D object (typed FeaturePython)
  Area = 0.664761
  FirstAngle = 0
  LastAngle = 0
  MakeFace = true
  Placement = pos=(-0.097,3.721,0) rot=(-1.209,5.934,1;0rad)
  Radius = 0.46
  expr: .Placement.Base.x = <<Spreadsheet>>.AWG_21_A_x
  expr: .Placement.Base.y = <<Spreadsheet>>.AWG_21_A_y
  expr: .Placement.Rotation.Axis.x = <<Spreadsheet>>.AWG_11_A_x
  expr: .Placement.Rotation.Axis.y = <<Spreadsheet>>.AWG_11_A_y
  expr: Radius = <<Spreadsheet>>.awg21_insulation_radius
FEATURE [Part::Part2DObjectPython] Circle064  label="Dielectric_015"  # Draft 2D object (typed FeaturePython)
  Area = 0.664761
  FirstAngle = 0
  LastAngle = 0
  MakeFace = true
  Placement = pos=(-3.221,-2.325,0) rot=(-1.209,5.934,1;0rad)
  Radius = 0.46
  expr: .Placement.Base.x = <<Spreadsheet>>.AWG_21_B_x
  expr: .Placement.Base.y = <<Spreadsheet>>.AWG_21_B_y
  expr: .Placement.Rotation.Axis.x = <<Spreadsheet>>.AWG_11_A_x
  expr: .Placement.Rotation.Axis.y = <<Spreadsheet>>.AWG_11_A_y
  expr: Radius = <<Spreadsheet>>.awg21_insulation_radius
FEATURE [Part::Part2DObjectPython] Circle065  label="Dielectric_016"  # Draft 2D object (typed FeaturePython)
  Area = 0.664761
  FirstAngle = 0
  LastAngle = 0
  MakeFace = true
  Placement = pos=(1.334,-1.359,0) rot=(-1.209,5.934,1;0rad)
  Radius = 0.46
  expr: .Placement.Base.x = <<Spreadsheet>>.AWG_21_C_x
  expr: .Placement.Base.y = <<Spreadsheet>>.AWG_21_C_y
  expr: .Placement.Rotation.Axis.x = <<Spreadsheet>>.AWG_11_A_x
  expr: .Placement.Rotation.Axis.y = <<Spreadsheet>>.AWG_11_A_y
  expr: Radius = <<Spreadsheet>>.awg21_insulation_radius
FEATURE [Part::Part2DObjectPython] Circle066  label="Dielectric_017"  # Draft 2D object (typed FeaturePython)
  Area = 0.664761
  FirstAngle = 0
  LastAngle = 0
  MakeFace = true
  Placement = pos=(3.588,1.443,0) rot=(-1.209,5.934,1;0rad)
  Radius = 0.46
  expr: .Placement.Base.x = <<Spreadsheet>>.AWG_21_D_x
  expr: .Placement.Base.y = <<Spreadsheet>>.AWG_21_D_y
  expr: .Placement.Rotation.Axis.x = <<Spreadsheet>>.AWG_11_A_x
  expr: .Placement.Rotation.Axis.y = <<Spreadsheet>>.AWG_11_A_y
  expr: Radius = <<Spreadsheet>>.awg21_insulation_radius
FEATURE [Part::Part2DObjectPython] Circle067  label="Dielectric_018"  # Draft 2D object (typed FeaturePython)
  Area = 0.664761
  FirstAngle = 0
  LastAngle = 0
  MakeFace = true
  Placement = pos=(4.578,0.203,0) rot=(-1.209,5.934,1;0rad)
  Radius = 0.46
  expr: .Placement.Base.x = <<Spreadsheet>>.AWG_21_E_x
  expr: .Placement.Base.y = <<Spreadsheet>>.AWG_21_E_y
  expr: .Placement.Rotation.Axis.x = <<Spreadsheet>>.AWG_11_A_x
  expr: .Placement.Rotation.Axis.y = <<Spreadsheet>>.AWG_11_A_y
  expr: Radius = <<Spreadsheet>>.awg21_insulation_radius
FEATURE [Part::Part2DObjectPython] Circle068  label="Dielectric_019"  # Draft 2D object (typed FeaturePython)
  Area = 0.664761
  FirstAngle = 0
  LastAngle = 0
  MakeFace = true
  Placement = pos=(4.399,-0.751,0) rot=(-1.209,5.934,1;0rad)
  Radius = 0.46
  expr: .Placement.Base.x = <<Spreadsheet>>.AWG_21_F_x
  expr: .Placement.Base.y = <<Spreadsheet>>.AWG_21_F_y
  expr: .Placement.Rotation.Axis.x = <<Spreadsheet>>.AWG_11_A_x
  expr: .Placement.Rotation.Axis.y = <<Spreadsheet>>.AWG_11_A_y
  expr: Radius = <<Spreadsheet>>.awg21_insulation_radius
FEATURE [Part::Part2DObjectPython] Circle069  label="Dielectric_020"  # Draft 2D object (typed FeaturePython)
  Area = 0.664761
  FirstAngle = 0
  LastAngle = 0
  MakeFace = true
  Placement = pos=(2.658,-1.24,0) rot=(-1.209,5.934,1;0rad)
  Radius = 0.46
  expr: .Placement.Base.x = <<Spreadsheet>>.AWG_21_G_x
  expr: .Placement.Base.y = <<Spreadsheet>>.AWG_21_G_y
  expr: .Placement.Rotation.Axis.x = <<Spreadsheet>>.AWG_11_A_x
  expr: .Placement.Rotation.Axis.y = <<Spreadsheet>>.AWG_11_A_y
  expr: Radius = <<Spreadsheet>>.awg21_insulation_radius
FEATURE [Part::Part2DObjectPython] Circle070  label="Dielectric_021"  # Draft 2D object (typed FeaturePython)
  Area = 0.664761
  FirstAngle = 0
  LastAngle = 0
  MakeFace = true
  Placement = pos=(3.779,-1.86,0) rot=(-1.209,5.934,1;0rad)
  Radius = 0.46
  expr: .Placement.Base.x = <<Spreadsheet>>.AWG_21_H_x
  expr: .Placement.Base.y = <<Spreadsheet>>.AWG_21_H_y
  expr: .Placement.Rotation.Axis.x = <<Spreadsheet>>.AWG_11_A_x
  expr: .Placement.Rotation.Axis.y = <<Spreadsheet>>.AWG_11_A_y
  expr: Radius = <<Spreadsheet>>.awg21_insulation_radius
FEATURE [Part::Part2DObjectPython] Circle071  label="Dielectric_022"  # Draft 2D object (typed FeaturePython)
  Area = 0.664761
  FirstAngle = 0
  LastAngle = 0
  MakeFace = true
  Placement = pos=(4.876,-2.552,0) rot=(-1.209,5.934,1;0rad)
  Radius = 0.46
  expr: .Placement.Base.x = <<Spreadsheet>>.AWG_21_I_x
  expr: .Placement.Base.y = <<Spreadsheet>>.AWG_21_I_y
  expr: .Placement.Rotation.Axis.x = <<Spreadsheet>>.AWG_11_A_x
  expr: .Placement.Rotation.Axis.y = <<Spreadsheet>>.AWG_11_A_y
  expr: Radius = <<Spreadsheet>>.awg21_insulation_radius
FEATURE [Part::Part2DObjectPython] Circle072  label="Dielectric_023"  # Draft 2D object (typed FeaturePython)
  Area = 0.664761
  FirstAngle = 0
  LastAngle = 0
  MakeFace = true
  Placement = pos=(6.235,-2.623,0) rot=(-1.209,5.934,1;0rad)
  Radius = 0.46
  expr: .Placement.Base.x = <<Spreadsheet>>.AWG_21_J_x
  expr: .Placement.Base.y = <<Spreadsheet>>.AWG_21_J_y
  expr: .Placement.Rotation.Axis.x = <<Spreadsheet>>.AWG_11_A_x
  expr: .Placement.Rotation.Axis.y = <<Spreadsheet>>.AWG_11_A_y
  expr: Radius = <<Spreadsheet>>.awg21_insulation_radius
FEATURE [Part::Part2DObjectPython] Circle073  label="Dielectric_024"  # Draft 2D object (typed FeaturePython)
  Area = 0.664761
  FirstAngle = 0
  LastAngle = 0
  MakeFace = true
  Placement = pos=(5.961,-3.661,0) rot=(-1.209,5.934,1;0rad)
  Radius = 0.46
  expr: .Placement.Base.x = <<Spreadsheet>>.AWG_21_K_x
  expr: .Placement.Base.y = <<Spreadsheet>>.AWG_21_K_y
  expr: .Placement.Rotation.Axis.x = <<Spreadsheet>>.AWG_11_A_x
  expr: .Placement.Rotation.Axis.y = <<Spreadsheet>>.AWG_11_A_y
  expr: Radius = <<Spreadsheet>>.awg21_insulation_radius
FEATURE [Part::Part2DObjectPython] Circle074  label="Dielectric_025"  # Draft 2D object (typed FeaturePython)
  Area = 1.6513
  FirstAngle = 0
  LastAngle = 0
  MakeFace = true
  Placement = pos=(0.929,6.547,0) rot=(-1.209,5.934,1;0rad)
  Radius = 0.725
  expr: .Placement.Base.x = <<Spreadsheet>>.AWG_17_A_x
  expr: .Placement.Base.y = <<Spreadsheet>>.AWG_17_A_y
  expr: .Placement.Rotation.Axis.x = <<Spreadsheet>>.AWG_11_A_x
  expr: .Placement.Rotation.Axis.y = <<Spreadsheet>>.AWG_11_A_y
  expr: Radius = <<Spreadsheet>>.awg17_insulation_radius
FEATURE [Part::Part2DObjectPython] Circle075  label="Dielectric_026"  # Draft 2D object (typed FeaturePython)
  Area = 1.6513
  FirstAngle = 0
  LastAngle = 0
  MakeFace = true
  Placement = pos=(2.562,6.213,0) rot=(-1.209,5.934,1;0rad)
  Radius = 0.725
  expr: .Placement.Base.x = <<Spreadsheet>>.AWG_17_B_x
  expr: .Placement.Base.y = <<Spreadsheet>>.AWG_17_B_y
  expr: .Placement.Rotation.Axis.x = <<Spreadsheet>>.AWG_11_A_x
  expr: .Placement.Rotation.Axis.y = <<Spreadsheet>>.AWG_11_A_y
  expr: Radius = <<Spreadsheet>>.awg17_insulation_radius
FEATURE [Part::Part2DObjectPython] Circle076  label="Dielectric_027"  # Draft 2D object (typed FeaturePython)
  Area = 1.6513
  FirstAngle = 0
  LastAngle = 0
  MakeFace = true
  Placement = pos=(1.012,4.866,0) rot=(-1.209,5.934,1;0rad)
  Radius = 0.725
  expr: .Placement.Base.x = <<Spreadsheet>>.AWG_17_C_x
  expr: .Placement.Base.y = <<Spreadsheet>>.AWG_17_C_y
  expr: .Placement.Rotation.Axis.x = <<Spreadsheet>>.AWG_11_A_x
  expr: .Placement.Rotation.Axis.y = <<Spreadsheet>>.AWG_11_A_y
  expr: Radius = <<Spreadsheet>>.awg17_insulation_radius
FEATURE [Part::Part2DObjectPython] Circle077  label="Dielectric_028"  # Draft 2D object (typed FeaturePython)
  Area = 1.6513
  FirstAngle = 0
  LastAngle = 0
  MakeFace = true
  Placement = pos=(2.562,0.251,0) rot=(-1.209,5.934,1;0rad)
  Radius = 0.725
  expr: .Placement.Base.x = <<Spreadsheet>>.AWG_17_D_x
  expr: .Placement.Base.y = <<Spreadsheet>>.AWG_17_D_y
  expr: .Placement.Rotation.Axis.x = <<Spreadsheet>>.AWG_11_A_x
  expr: .Placement.Rotation.Axis.y = <<Spreadsheet>>.AWG_11_A_y
  expr: Radius = <<Spreadsheet>>.awg17_insulation_radius
FEATURE [Part::Part2DObjectPython] Circle078  label="Dielectric_029"  # Draft 2D object (typed FeaturePython)
  Area = 1.6513
  FirstAngle = 0
  LastAngle = 0
  MakeFace = true
  Placement = pos=(-1.087,-6.535,0) rot=(-1.209,5.934,1;0rad)
  Radius = 0.725
  expr: .Placement.Base.x = <<Spreadsheet>>.AWG_17_E_x
  expr: .Placement.Base.y = <<Spreadsheet>>.AWG_17_E_y
  expr: .Placement.Rotation.Axis.x = <<Spreadsheet>>.AWG_11_A_x
  expr: .Placement.Rotation.Axis.y = <<Spreadsheet>>.AWG_11_A_y
  expr: Radius = <<Spreadsheet>>.awg17_insulation_radius
FEATURE [Part::Part2DObjectPython] Circle080  label="OpenBoundary_0"  # Draft 2D object (typed FeaturePython)
  Area = 7853.98
  FirstAngle = 0
  LastAngle = 0
  MakeFace = true
  Radius = 50
  expr: .Placement.Rotation.Axis.x = <<Spreadsheet>>.AWG_11_A_x
  expr: .Placement.Rotation.Axis.y = <<Spreadsheet>>.AWG_11_A_y
FEATURE [Part::Part2DObjectPython] Rectangle001  label="Inner_region_box"  # Draft 2D object (typed FeaturePython)
  Area = 900
  ChamferSize = 0
  Columns = 1
  FilletRadius = 0
  Height = 30
  Length = 30
  MakeFace = true
  Placement = pos=(-16.209,-9.066,0) rot=(0,0,1;0rad)
  Rows = 1
  expr: .Placement.Base.x = <<Spreadsheet>>.AWG_11_A_x - <<Spreadsheet>>.fdtd_cell_Lx / 2
  expr: .Placement.Base.y = <<Spreadsheet>>.AWG_11_A_y - <<Spreadsheet>>.FDTD_Cell_Ly / 2
  expr: Height = <<Spreadsheet>>.FDTD_Cell_Ly
  expr: Length = <<Spreadsheet>>.fdtd_cell_Lx
FEATURE [Part::Part2DObjectPython] Circle081  label="Overbraid_internal001"  # Draft 2D object (typed FeaturePython)
  Area = 203.583
  FirstAngle = 0
  LastAngle = 0
  MakeFace = true
  Radius = 8.05
  expr: Radius = <<Spreadsheet>>.OJ_outer_radius
FEATURE [Part::Part2DObjectPython] Circle082  label="Dielectric_031"  # Draft 2D object (typed FeaturePython)
  Area = 4.90874
  FirstAngle = 0
  LastAngle = 0
  MakeFace = true
  Placement = pos=(-1.209,5.934,0) rot=(-1.209,5.934,1;0rad)
  Radius = 1.25
  expr: .Placement.Base.x = <<Spreadsheet>>.AWG_11_A_x
  expr: .Placement.Base.y = <<Spreadsheet>>.AWG_11_A_y
  expr: .Placement.Rotation.Axis.x = <<Spreadsheet>>.AWG_11_A_x
  expr: .Placement.Rotation.Axis.y = <<Spreadsheet>>.AWG_11_A_y
  expr: Radius = <<Spreadsheet>>.awg11_insulation_radius
FEATURE [Part::Part2DObjectPython] Circle083  label="Dielectric_032"  # Draft 2D object (typed FeaturePython)
  Area = 4.90874
  FirstAngle = 0
  LastAngle = 0
  MakeFace = true
  Placement = pos=(-3.734,4.83,0) rot=(-1.209,5.934,1;0rad)
  Radius = 1.25
  expr: .Placement.Base.x = <<Spreadsheet>>.AWG_11_B_x
  expr: .Placement.Base.y = <<Spreadsheet>>.AWG_11_B_y
  expr: .Placement.Rotation.Axis.x = <<Spreadsheet>>.AWG_11_A_x
  expr: .Placement.Rotation.Axis.y = <<Spreadsheet>>.AWG_11_A_y
  expr: Radius = <<Spreadsheet>>.awg11_insulation_radius
FEATURE [Part::Part2DObjectPython] Circle084  label="Dielectric_033"  # Draft 2D object (typed FeaturePython)
  Area = 4.90874
  FirstAngle = 0
  LastAngle = 0
  MakeFace = true
  Placement = pos=(-5.595,2.349,0) rot=(-1.209,5.934,1;0rad)
  Radius = 1.25
  expr: .Placement.Base.x = <<Spreadsheet>>.AWG_11_C_x
  expr: .Placement.Base.y = <<Spreadsheet>>.AWG_11_C_y
  expr: .Placement.Rotation.Axis.x = <<Spreadsheet>>.AWG_11_A_x
  expr: .Placement.Rotation.Axis.y = <<Spreadsheet>>.AWG_11_A_y
  expr: Radius = <<Spreadsheet>>.awg11_insulation_radius
FEATURE [Part::Part2DObjectPython] Circle085  label="Dielectric_034"  # Draft 2D object (typed FeaturePython)
  Area = 4.90874
  FirstAngle = 0
  LastAngle = 0
  MakeFace = true
  Placement = pos=(-5.905,-0.548,0) rot=(-1.209,5.934,1;0rad)
  Radius = 1.25
  expr: .Placement.Base.x = <<Spreadsheet>>.AWG_11_D_x
  expr: .Placement.Base.y = <<Spreadsheet>>.AWG_11_D_y
  expr: .Placement.Rotation.Axis.x = <<Spreadsheet>>.AWG_11_A_x
  expr: .Placement.Rotation.Axis.y = <<Spreadsheet>>.AWG_11_A_y
  expr: Radius = <<Spreadsheet>>.awg11_insulation_radius
FEATURE [Part::Part2DObjectPython] Circle086  label="Dielectric_035"  # Draft 2D object (typed FeaturePython)
  Area = 4.90874
  FirstAngle = 0
  LastAngle = 0
  MakeFace = true
  Placement = pos=(-5.141,-3.16,0) rot=(-1.209,5.934,1;0rad)
  Radius = 1.25
  expr: .Placement.Base.x = <<Spreadsheet>>.AWG_11_E_x
  expr: .Placement.Base.y = <<Spreadsheet>>.AWG_11_E_y
  expr: .Placement.Rotation.Axis.x = <<Spreadsheet>>.AWG_11_A_x
  expr: .Placement.Rotation.Axis.y = <<Spreadsheet>>.AWG_11_A_y
  expr: Radius = <<Spreadsheet>>.awg11_insulation_radius
FEATURE [Part::Part2DObjectPython] Circle087  label="Dielectric_036"  # Draft 2D object (typed FeaturePython)
  Area = 4.90874
  FirstAngle = 0
  LastAngle = 0
  MakeFace = true
  Placement = pos=(-2.923,-5.378,0) rot=(-1.209,5.934,1;0rad)
  Radius = 1.25
  expr: .Placement.Base.x = <<Spreadsheet>>.AWG_11_F_x
  expr: .Placement.Base.y = <<Spreadsheet>>.AWG_11_F_y
  expr: .Placement.Rotation.Axis.x = <<Spreadsheet>>.AWG_11_A_x
  expr: .Placement.Rotation.Axis.y = <<Spreadsheet>>.AWG_11_A_y
  expr: Radius = <<Spreadsheet>>.awg11_insulation_radius
FEATURE [Part::Part2DObjectPython] Circle088  label="Dielectric_037"  # Draft 2D object (typed FeaturePython)
  Area = 4.90874
  FirstAngle = 0
  LastAngle = 0
  MakeFace = true
  Placement = pos=(6.545,-0.417,0) rot=(-1.209,5.934,1;0rad)
  Radius = 1.25
  expr: .Placement.Base.x = <<Spreadsheet>>.AWG_11_G_x
  expr: .Placement.Base.y = <<Spreadsheet>>.AWG_11_G_y
  expr: .Placement.Rotation.Axis.x = <<Spreadsheet>>.AWG_11_A_x
  expr: .Placement.Rotation.Axis.y = <<Spreadsheet>>.AWG_11_A_y
  expr: Radius = <<Spreadsheet>>.awg11_insulation_radius
FEATURE [Part::Part2DObjectPython] Circle089  label="Dielectric_038"  # Draft 2D object (typed FeaturePython)
  Area = 4.90874
  FirstAngle = 0
  LastAngle = 0
  MakeFace = true
  Placement = pos=(5.699,2.671,0) rot=(-1.209,5.934,1;0rad)
  Radius = 1.25
  expr: .Placement.Base.x = <<Spreadsheet>>.AWG_11_H_x
  expr: .Placement.Base.y = <<Spreadsheet>>.AWG_11_H_y
  expr: .Placement.Rotation.Axis.x = <<Spreadsheet>>.AWG_11_A_x
  expr: .Placement.Rotation.Axis.y = <<Spreadsheet>>.AWG_11_A_y
  expr: Radius = <<Spreadsheet>>.awg11_insulation_radius
FEATURE [Part::Part2DObjectPython] Circle090  label="Dielectric_039"  # Draft 2D object (typed FeaturePython)
  Area = 4.90874
  FirstAngle = 0
  LastAngle = 0
  MakeFace = true
  Placement = pos=(3.767,4.46,0) rot=(-1.209,5.934,1;0rad)
  Radius = 1.25
  expr: .Placement.Base.x = <<Spreadsheet>>.AWG_11_I_x
  expr: .Placement.Base.y = <<Spreadsheet>>.AWG_11_I_y
  expr: .Placement.Rotation.Axis.x = <<Spreadsheet>>.AWG_11_A_x
  expr: .Placement.Rotation.Axis.y = <<Spreadsheet>>.AWG_11_A_y
  expr: Radius = <<Spreadsheet>>.awg11_insulation_radius
FEATURE [Part::Part2DObjectPython] Circle091  label="Dielectric_040"  # Draft 2D object (typed FeaturePython)
  Area = 4.90874
  FirstAngle = 0
  LastAngle = 0
  MakeFace = true
  Placement = pos=(1.763,2.457,0) rot=(-1.209,5.934,1;0rad)
  Radius = 1.25
  expr: .Placement.Base.x = <<Spreadsheet>>.AWG_11_J_x
  expr: .Placement.Base.y = <<Spreadsheet>>.AWG_11_J_y
  expr: .Placement.Rotation.Axis.x = <<Spreadsheet>>.AWG_11_A_x
  expr: .Placement.Rotation.Axis.y = <<Spreadsheet>>.AWG_11_A_y
  expr: Radius = <<Spreadsheet>>.awg11_insulation_radius
FEATURE [Part::Part2DObjectPython] Circle092  label="Dielectric_041"  # Draft 2D object (typed FeaturePython)
  Area = 4.90874
  FirstAngle = 0
  LastAngle = 0
  MakeFace = true
  Placement = pos=(0.022,0.358,0) rot=(-1.209,5.934,1;0rad)
  Radius = 1.25
  expr: .Placement.Base.x = <<Spreadsheet>>.AWG_11_K_x
  expr: .Placement.Base.y = <<Spreadsheet>>.AWG_11_K_y
  expr: .Placement.Rotation.Axis.x = <<Spreadsheet>>.AWG_11_A_x
  expr: .Placement.Rotation.Axis.y = <<Spreadsheet>>.AWG_11_A_y
  expr: Radius = <<Spreadsheet>>.awg11_insulation_radius
FEATURE [Part::Part2DObjectPython] Circle093  label="Dielectric_042"  # Draft 2D object (typed FeaturePython)
  Area = 4.90874
  FirstAngle = 0
  LastAngle = 0
  MakeFace = true
  Placement = pos=(-1.015,-2.337,0) rot=(-1.209,5.934,1;0rad)
  Radius = 1.25
  expr: .Placement.Base.x = <<Spreadsheet>>.AWG_11_L_x
  expr: .Placement.Base.y = <<Spreadsheet>>.AWG_11_L_y
  expr: .Placement.Rotation.Axis.x = <<Spreadsheet>>.AWG_11_A_x
  expr: .Placement.Rotation.Axis.y = <<Spreadsheet>>.AWG_11_A_y
  expr: Radius = <<Spreadsheet>>.awg11_insulation_radius
FEATURE [Part::Part2DObjectPython] Circle094  label="Dielectric_043"  # Draft 2D object (typed FeaturePython)
  Area = 4.90874
  FirstAngle = 0
  LastAngle = 0
  MakeFace = true
  Placement = pos=(-2.983,-0.036,0) rot=(-1.209,5.934,1;0rad)
  Radius = 1.25
  expr: .Placement.Base.x = <<Spreadsheet>>.AWG_11_M_x
  expr: .Placement.Base.y = <<Spreadsheet>>.AWG_11_M_y
  expr: .Placement.Rotation.Axis.x = <<Spreadsheet>>.AWG_11_A_x
  expr: .Placement.Rotation.Axis.y = <<Spreadsheet>>.AWG_11_A_y
  expr: Radius = <<Spreadsheet>>.awg11_insulation_radius
FEATURE [Part::Part2DObjectPython] Circle095  label="Dielectric_044"  # Draft 2D object (typed FeaturePython)
  Area = 4.90874
  FirstAngle = 0
  LastAngle = 0
  MakeFace = true
  Placement = pos=(-1.683,2.314,0) rot=(-1.209,5.934,1;0rad)
  Radius = 1.25
  expr: .Placement.Base.x = <<Spreadsheet>>.AWG_11_N_x
  expr: .Placement.Base.y = <<Spreadsheet>>.AWG_11_N_y
  expr: .Placement.Rotation.Axis.x = <<Spreadsheet>>.AWG_11_A_x
  expr: .Placement.Rotation.Axis.y = <<Spreadsheet>>.AWG_11_A_y
  expr: Radius = <<Spreadsheet>>.awg11_insulation_radius
FEATURE [Part::Part2DObjectPython] Circle096  label="Overbraid_external001"  # Draft 2D object (typed FeaturePython)
  Area = 198.557
  FirstAngle = 0
  LastAngle = 0
  MakeFace = true
  Radius = 7.95
  expr: Radius = <<Spreadsheet>>.OJ_radius
FEATURE [Part::Part2DObjectPython] Circle097  label="Dielectric_045"  # Draft 2D object (typed FeaturePython)
  Area = 0.664761
  FirstAngle = 0
  LastAngle = 0
  MakeFace = true
  Placement = pos=(-0.097,3.721,0) rot=(-1.209,5.934,1;0rad)
  Radius = 0.46
  expr: .Placement.Base.x = <<Spreadsheet>>.AWG_21_A_x
  expr: .Placement.Base.y = <<Spreadsheet>>.AWG_21_A_y
  expr: .Placement.Rotation.Axis.x = <<Spreadsheet>>.AWG_11_A_x
  expr: .Placement.Rotation.Axis.y = <<Spreadsheet>>.AWG_11_A_y
  expr: Radius = <<Spreadsheet>>.awg21_insulation_radius
FEATURE [Part::Part2DObjectPython] Circle098  label="Dielectric_046"  # Draft 2D object (typed FeaturePython)
  Area = 0.664761
  FirstAngle = 0
  LastAngle = 0
  MakeFace = true
  Placement = pos=(-3.221,-2.325,0) rot=(-1.209,5.934,1;0rad)
  Radius = 0.46
  expr: .Placement.Base.x = <<Spreadsheet>>.AWG_21_B_x
  expr: .Placement.Base.y = <<Spreadsheet>>.AWG_21_B_y
  expr: .Placement.Rotation.Axis.x = <<Spreadsheet>>.AWG_11_A_x
  expr: .Placement.Rotation.Axis.y = <<Spreadsheet>>.AWG_11_A_y
  expr: Radius = <<Spreadsheet>>.awg21_insulation_radius
FEATURE [Part::Part2DObjectPython] Circle099  label="Dielectric_047"  # Draft 2D object (typed FeaturePython)
  Area = 0.664761
  FirstAngle = 0
  LastAngle = 0
  MakeFace = true
  Placement = pos=(1.334,-1.359,0) rot=(-1.209,5.934,1;0rad)
  Radius = 0.46
  expr: .Placement.Base.x = <<Spreadsheet>>.AWG_21_C_x
  expr: .Placement.Base.y = <<Spreadsheet>>.AWG_21_C_y
  expr: .Placement.Rotation.Axis.x = <<Spreadsheet>>.AWG_11_A_x
  expr: .Placement.Rotation.Axis.y = <<Spreadsheet>>.AWG_11_A_y
  expr: Radius = <<Spreadsheet>>.awg21_insulation_radius
FEATURE [Part::Part2DObjectPython] Circle100  label="Dielectric_048"  # Draft 2D object (typed FeaturePython)
  Area = 0.664761
  FirstAngle = 0
  LastAngle = 0
  MakeFace = true
  Placement = pos=(3.588,1.443,0) rot=(-1.209,5.934,1;0rad)
  Radius = 0.46
  expr: .Placement.Base.x = <<Spreadsheet>>.AWG_21_D_x
  expr: .Placement.Base.y = <<Spreadsheet>>.AWG_21_D_y
  expr: .Placement.Rotation.Axis.x = <<Spreadsheet>>.AWG_11_A_x
  expr: .Placement.Rotation.Axis.y = <<Spreadsheet>>.AWG_11_A_y
  expr: Radius = <<Spreadsheet>>.awg21_insulation_radius
FEATURE [Part::Part2DObjectPython] Circle101  label="Dielectric_049"  # Draft 2D object (typed FeaturePython)
  Area = 0.664761
  FirstAngle = 0
  LastAngle = 0
  MakeFace = true
  Placement = pos=(4.578,0.203,0) rot=(-1.209,5.934,1;0rad)
  Radius = 0.46
  expr: .Placement.Base.x = <<Spreadsheet>>.AWG_21_E_x
  expr: .Placement.Base.y = <<Spreadsheet>>.AWG_21_E_y
  expr: .Placement.Rotation.Axis.x = <<Spreadsheet>>.AWG_11_A_x
  expr: .Placement.Rotation.Axis.y = <<Spreadsheet>>.AWG_11_A_y
  expr: Radius = <<Spreadsheet>>.awg21_insulation_radius
FEATURE [Part::Part2DObjectPython] Circle102  label="Dielectric_050"  # Draft 2D object (typed FeaturePython)
  Area = 0.664761
  FirstAngle = 0
  LastAngle = 0
  MakeFace = true
  Placement = pos=(4.399,-0.751,0) rot=(-1.209,5.934,1;0rad)
  Radius = 0.46
  expr: .Placement.Base.x = <<Spreadsheet>>.AWG_21_F_x
  expr: .Placement.Base.y = <<Spreadsheet>>.AWG_21_F_y
  expr: .Placement.Rotation.Axis.x = <<Spreadsheet>>.AWG_11_A_x
  expr: .Placement.Rotation.Axis.y = <<Spreadsheet>>.AWG_11_A_y
  expr: Radius = <<Spreadsheet>>.awg21_insulation_radius
FEATURE [Part::Part2DObjectPython] Circle103  label="Dielectric_051"  # Draft 2D object (typed FeaturePython)
  Area = 0.664761
  FirstAngle = 0
  LastAngle = 0
  MakeFace = true
  Placement = pos=(2.658,-1.24,0) rot=(-1.209,5.934,1;0rad)
  Radius = 0.46
  expr: .Placement.Base.x = <<Spreadsheet>>.AWG_21_G_x
  expr: .Placement.Base.y = <<Spreadsheet>>.AWG_21_G_y
  expr: .Placement.Rotation.Axis.x = <<Spreadsheet>>.AWG_11_A_x
  expr: .Placement.Rotation.Axis.y = <<Spreadsheet>>.AWG_11_A_y
  expr: Radius = <<Spreadsheet>>.awg21_insulation_radius
FEATURE [Part::Part2DObjectPython] Circle104  label="Dielectric_052"  # Draft 2D object (typed FeaturePython)
  Area = 0.664761
  FirstAngle = 0
  LastAngle = 0
  MakeFace = true
  Placement = pos=(3.779,-1.86,0) rot=(-1.209,5.934,1;0rad)
  Radius = 0.46
  expr: .Placement.Base.x = <<Spreadsheet>>.AWG_21_H_x
  expr: .Placement.Base.y = <<Spreadsheet>>.AWG_21_H_y
  expr: .Placement.Rotation.Axis.x = <<Spreadsheet>>.AWG_11_A_x
  expr: .Placement.Rotation.Axis.y = <<Spreadsheet>>.AWG_11_A_y
  expr: Radius = <<Spreadsheet>>.awg21_insulation_radius
FEATURE [Part::Part2DObjectPython] Circle105  label="Dielectric_053"  # Draft 2D object (typed FeaturePython)
  Area = 0.664761
  FirstAngle = 0
  LastAngle = 0
  MakeFace = true
  Placement = pos=(4.876,-2.552,0) rot=(-1.209,5.934,1;0rad)
  Radius = 0.46
  expr: .Placement.Base.x = <<Spreadsheet>>.AWG_21_I_x
  expr: .Placement.Base.y = <<Spreadsheet>>.AWG_21_I_y
  expr: .Placement.Rotation.Axis.x = <<Spreadsheet>>.AWG_11_A_x
  expr: .Placement.Rotation.Axis.y = <<Spreadsheet>>.AWG_11_A_y
  expr: Radius = <<Spreadsheet>>.awg21_insulation_radius
FEATURE [Part::Part2DObjectPython] Circle106  label="Dielectric_054"  # Draft 2D object (typed FeaturePython)
  Area = 0.664761
  FirstAngle = 0
  LastAngle = 0
  MakeFace = true
  Placement = pos=(6.235,-2.623,0) rot=(-1.209,5.934,1;0rad)
  Radius = 0.46
  expr: .Placement.Base.x = <<Spreadsheet>>.AWG_21_J_x
  expr: .Placement.Base.y = <<Spreadsheet>>.AWG_21_J_y
  expr: .Placement.Rotation.Axis.x = <<Spreadsheet>>.AWG_11_A_x
  expr: .Placement.Rotation.Axis.y = <<Spreadsheet>>.AWG_11_A_y
  expr: Radius = <<Spreadsheet>>.awg21_insulation_radius
FEATURE [Part::Part2DObjectPython] Circle107  label="Dielectric_055"  # Draft 2D object (typed FeaturePython)
  Area = 0.664761
  FirstAngle = 0
  LastAngle = 0
  MakeFace = true
  Placement = pos=(5.961,-3.661,0) rot=(-1.209,5.934,1;0rad)
  Radius = 0.46
  expr: .Placement.Base.x = <<Spreadsheet>>.AWG_21_K_x
  expr: .Placement.Base.y = <<Spreadsheet>>.AWG_21_K_y
  expr: .Placement.Rotation.Axis.x = <<Spreadsheet>>.AWG_11_A_x
  expr: .Placement.Rotation.Axis.y = <<Spreadsheet>>.AWG_11_A_y
  expr: Radius = <<Spreadsheet>>.awg21_insulation_radius
FEATURE [Part::Part2DObjectPython] Circle108  label="Dielectric_056"  # Draft 2D object (typed FeaturePython)
  Area = 1.6513
  FirstAngle = 0
  LastAngle = 0
  MakeFace = true
  Placement = pos=(0.929,6.547,0) rot=(-1.209,5.934,1;0rad)
  Radius = 0.725
  expr: .Placement.Base.x = <<Spreadsheet>>.AWG_17_A_x
  expr: .Placement.Base.y = <<Spreadsheet>>.AWG_17_A_y
  expr: .Placement.Rotation.Axis.x = <<Spreadsheet>>.AWG_11_A_x
  expr: .Placement.Rotation.Axis.y = <<Spreadsheet>>.AWG_11_A_y
  expr: Radius = <<Spreadsheet>>.awg17_insulation_radius
FEATURE [Part::Part2DObjectPython] Circle109  label="Dielectric_057"  # Draft 2D object (typed FeaturePython)
  Area = 1.6513
  FirstAngle = 0
  LastAngle = 0
  MakeFace = true
  Placement = pos=(2.562,6.213,0) rot=(-1.209,5.934,1;0rad)
  Radius = 0.725
  expr: .Placement.Base.x = <<Spreadsheet>>.AWG_17_B_x
  expr: .Placement.Base.y = <<Spreadsheet>>.AWG_17_B_y
  expr: .Placement.Rotation.Axis.x = <<Spreadsheet>>.AWG_11_A_x
  expr: .Placement.Rotation.Axis.y = <<Spreadsheet>>.AWG_11_A_y
  expr: Radius = <<Spreadsheet>>.awg17_insulation_radius
FEATURE [Part::Part2DObjectPython] Circle110  label="Dielectric_058"  # Draft 2D object (typed FeaturePython)
  Area = 1.6513
  FirstAngle = 0
  LastAngle = 0
  MakeFace = true
  Placement = pos=(1.012,4.866,0) rot=(-1.209,5.934,1;0rad)
  Radius = 0.725
  expr: .Placement.Base.x = <<Spreadsheet>>.AWG_17_C_x
  expr: .Placement.Base.y = <<Spreadsheet>>.AWG_17_C_y
  expr: .Placement.Rotation.Axis.x = <<Spreadsheet>>.AWG_11_A_x
  expr: .Placement.Rotation.Axis.y = <<Spreadsheet>>.AWG_11_A_y
  expr: Radius = <<Spreadsheet>>.awg17_insulation_radius
FEATURE [Part::Part2DObjectPython] Circle111  label="Dielectric_059"  # Draft 2D object (typed FeaturePython)
  Area = 1.6513
  FirstAngle = 0
  LastAngle = 0
  MakeFace = true
  Placement = pos=(2.562,0.251,0) rot=(-1.209,5.934,1;0rad)
  Radius = 0.725
  expr: .Placement.Base.x = <<Spreadsheet>>.AWG_17_D_x
  expr: .Placement.Base.y = <<Spreadsheet>>.AWG_17_D_y
  expr: .Placement.Rotation.Axis.x = <<Spreadsheet>>.AWG_11_A_x
  expr: .Placement.Rotation.Axis.y = <<Spreadsheet>>.AWG_11_A_y
  expr: Radius = <<Spreadsheet>>.awg17_insulation_radius
FEATURE [Part::Part2DObjectPython] Circle112  label="Dielectric_060"  # Draft 2D object (typed FeaturePython)
  Area = 1.6513
  FirstAngle = 0
  LastAngle = 0
  MakeFace = true
  Placement = pos=(-1.087,-6.535,0) rot=(-1.209,5.934,1;0rad)
  Radius = 0.725
  expr: .Placement.Base.x = <<Spreadsheet>>.AWG_17_E_x
  expr: .Placement.Base.y = <<Spreadsheet>>.AWG_17_E_y
  expr: .Placement.Rotation.Axis.x = <<Spreadsheet>>.AWG_11_A_x
  expr: .Placement.Rotation.Axis.y = <<Spreadsheet>>.AWG_11_A_y
  expr: Radius = <<Spreadsheet>>.awg17_insulation_radius
FEATURE [Part::Cut] Cut001  label="Dielectric_061"
  Base = -> Circle081
  Tool = -> Circle096
FEATURE [Part::MultiFuse] Fusion
  Shapes = -> [Circle082,Circle083,Circle084,Circle085,Circle086,Circle087,Circle088,Circle089,Circle090,Circle091,Circle092,Circle093,Circle094,Circle095,Circle097,Circle098,Circle099,Circle100,Circle101,Circle102,Circle103,Circle104,Circle105,Circle106,Circle107,Circle108,Circle109,Circle110,Circle111,Circle112,Cut001]
FEATURE [Part::Cut] Cut002  label="fdtd_cell"
  Base = -> Rectangle001
  Tool = -> Fusion
FEATURE [Part::Part2DObjectPython] Rectangle  label="inner_region"  # Draft 2D object (typed FeaturePython)
  Area = 272.25
  ChamferSize = 0
  Columns = 1
  FilletRadius = 0
  Height = 16.5
  Length = 16.5
  MakeFace = true
  Placement = pos=(-8.25,-8.25,0) rot=(0,0,1;0rad)
  Rows = 1
  expr: .Placement.Base.x = -<<Spreadsheet>>.Inner_region_Dx / 2
  expr: .Placement.Base.y = -<<Spreadsheet>>.Inner_region_Dy / 2
  expr: Height = <<Spreadsheet>>.Inner_region_Dy
  expr: Length = <<Spreadsheet>>.Inner_region_Dx
